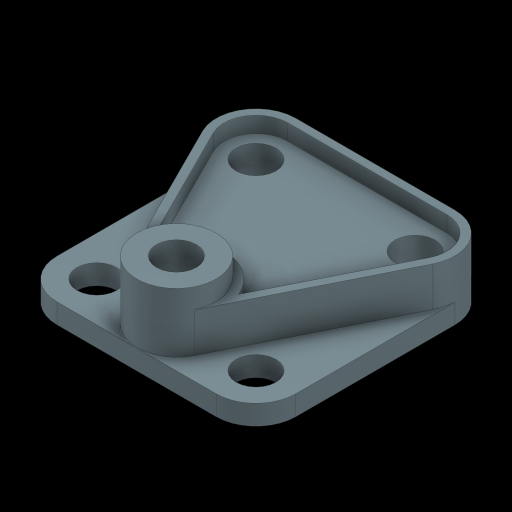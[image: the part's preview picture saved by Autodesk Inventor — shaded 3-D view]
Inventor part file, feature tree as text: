
AUTODESK INVENTOR PART (.ipt)
format: ipt  version: 2024 (Build 280153000, 153)  size: 209,920 bytes
history: native  units: in
note: dims shown in document units (in); Inventor stores cm internally (conversion verified against a paired STEP export)
features: extrude x4, sketch x1
ambient origin geometry x8: Origin, YZ Plane, XZ Plane, XY Plane, X Axis, Y Axis, Z Axis, Center Point
bodies: Solid1 (feature_tree)
feature tree (5):
  sketch  "Sketch1"  dims[d0=1.0in d1=0.5in d2=2.5in d3=3.0in d4=1.5in d5=0.5in d6=0.5in d7=0.1in d8=0.1in d9=0.1in d10=1.0in d11=0.1422in d12=0.25in d13=0.0in d14=0.3in d15=0.0in d16=0.5in d17=0.0in d18=0.75in d19=0.0in]
  extrude  "BASE"  Depth=0.5in
  extrude  "RAISED FLOOR"  Depth=2.5in
  extrude  "EDGE"  Depth=3.0in
  extrude  "COLLUMN"  Depth=1.5in
